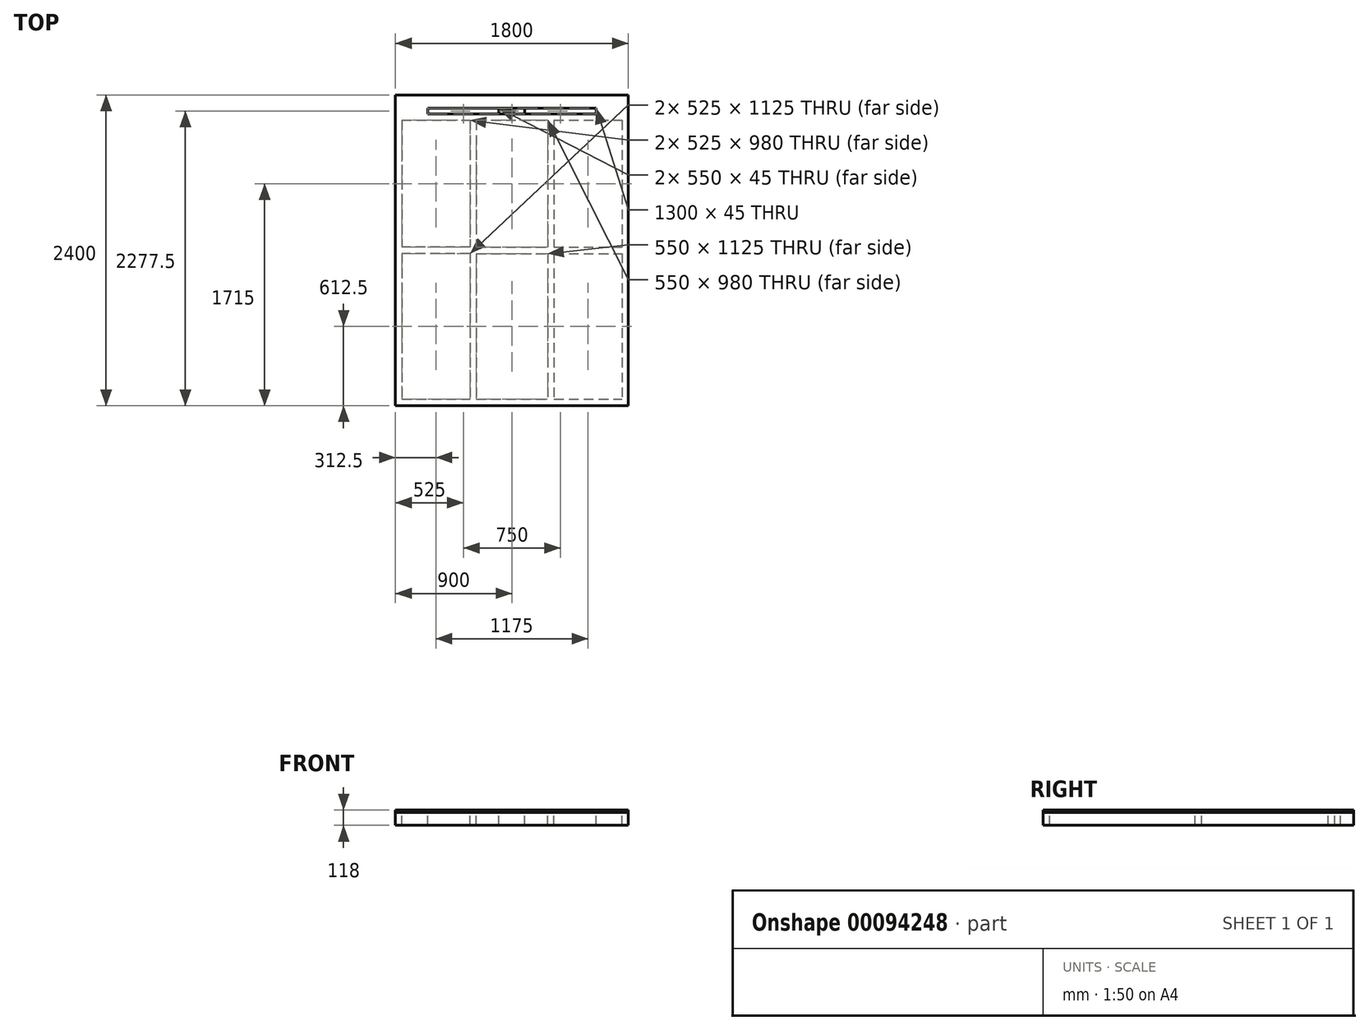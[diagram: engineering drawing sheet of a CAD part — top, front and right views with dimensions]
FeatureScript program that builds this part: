
annotation { "Feature Type Name" : "Feature", "Feature Type Description" : "" }
export const myFeature = defineFeature(function(context is Context, id is Id, definition is map)
    precondition{}
    {
        {
            var Q0;
            Q0=qCreatedBy(makeId("Top.planeOp"),FACE);
            var sketch = newSketch(context, id + "F0", { "sketchPlane" : qUnion([Q0])});
            skLineSegment(sketch, "E0.bottom", {"start": v(900, -1200) * mm, "end": v(-900, -1200) * mm});
            skLineSegment(sketch, "E0.top", {"start": v(900, 1200) * mm, "end": v(-900, 1200) * mm});
            skLineSegment(sketch, "E0.left", {"start": v(900, -1200) * mm, "end": v(900, 1200) * mm});
            skLineSegment(sketch, "E0.right", {"start": v(-900, -1200) * mm, "end": v(-900, 1200) * mm});
            skPoint(sketch, "E0.middle", {"position": v(0, 0) * mm});
            skLineSegment(sketch, "E1", {"start": v(-900, -1150) * mm, "end": v(900, -1150) * mm});
            skLineSegment(sketch, "E2", {"start": v(-900, 1150) * mm, "end": v(900, 1150) * mm});
            skLineSegment(sketch, "E3", {"start": v(-850, 1150) * mm, "end": v(-850, -1150) * mm});
            skLineSegment(sketch, "E4", {"start": v(-1110.96, 0) * mm, "end": v(1267.85, 0) * mm, "construction": true});
            skLineSegment(sketch, "E5", {"start": v(-325, 25) * mm, "end": v(-850, 25) * mm});
            skLineSegment(sketch, "E6", {"start": v(-325, -25) * mm, "end": v(-850, -25) * mm});
            skLineSegment(sketch, "E7", {"start": v(0, 1506.41) * mm, "end": v(0, -1337.08) * mm, "construction": true});
            skLineSegment(sketch, "E8", {"start": v(-275, 25) * mm, "end": v(0, 25) * mm});
            skLineSegment(sketch, "E9", {"start": v(-275, -25) * mm, "end": v(0, -25) * mm});
            skLineSegment(sketch, "E10", {"start": v(-300, 1299.82) * mm, "end": v(-300, -1330.47) * mm, "construction": true});
            skLineSegment(sketch, "E11.MirrorCS", {"start": v(300, 1299.82) * mm, "end": v(300, -1330.47) * mm, "construction": true});
            skLineSegment(sketch, "E12.MirrorCS", {"start": v(-275, 1005) * mm, "end": v(-275, -1150) * mm});
            skLineSegment(sketch, "E13.MirrorCS", {"start": v(275, 1005) * mm, "end": v(275, -1150) * mm});
            skLineSegment(sketch, "E14.MirrorCS", {"start": v(325, 1005) * mm, "end": v(325, -1150) * mm});
            skLineSegment(sketch, "E15.MirrorCS", {"start": v(275, 25) * mm, "end": v(0, 25) * mm});
            skLineSegment(sketch, "E16.MirrorCS", {"start": v(275, -25) * mm, "end": v(0, -25) * mm});
            skLineSegment(sketch, "E17.MirrorCS", {"start": v(325, -25) * mm, "end": v(850, -25) * mm});
            skLineSegment(sketch, "E18.MirrorCS", {"start": v(325, 25) * mm, "end": v(850, 25) * mm});
            skLineSegment(sketch, "E19.MirrorCS", {"start": v(850, 1150) * mm, "end": v(850, -1150) * mm});
            skLineSegment(sketch, "E20", {"start": v(-850, 1100) * mm, "end": v(850, 1100) * mm});
            skLineSegment(sketch, "E21", {"start": v(-850, 1055) * mm, "end": v(850, 1055) * mm});
            skLineSegment(sketch, "E22", {"start": v(-850, 1005) * mm, "end": v(850, 1005) * mm});
            skLineSegment(sketch, "E23", {"start": v(-650, 1055) * mm, "end": v(-650, 1100) * mm});
            skLineSegment(sketch, "E24.MirrorCS", {"start": v(650, 1055) * mm, "end": v(650, 1100) * mm});
            skLineSegment(sketch, "E25", {"start": v(-100, 1055) * mm, "end": v(-100, 1100) * mm});
            skLineSegment(sketch, "E26.MirrorCS", {"start": v(100, 1055) * mm, "end": v(100, 1100) * mm});
            skLineSegment(sketch, "E27.trimOffspring", {"start": v(-325, 1005) * mm, "end": v(-325, -1150) * mm});
            skSolve(sketch);
        }
        {
            var Q0;
            {var subQ4=sQuery(id+"F0.wireOp",EDGE,"E1");var subQ5=sQuery(id+"F0.wireOp",EDGE,"E0.left");var subQ6=makeQuery(id+"F0.imprint","INTERSECT",VERTEX,{"derivedFrom":[subQ5,subQ4]});Q0=makeQuery(id+"F0.imprint","IMPRINT",FACE,{"disambiguationData":[TD([[makeQuery(id+"F0.imprint","IMPRINT",EDGE,{"disambiguationData":[TD([[subQ6,-1.0]])],"derivedFrom":subQ5}),1.0]])]});}
            var Q1;
            {var subQ4=sQuery(id+"F0.wireOp",EDGE,"E0.bottom");Q1=makeQuery(id+"F0.imprint","IMPRINT",FACE,{"disambiguationData":[TD([[makeQuery(id+"F0.imprint","IMPRINT",EDGE,{"derivedFrom":subQ4}),-1.0]])]});}
            var Q2;
            {var subQ4=sQuery(id+"F0.wireOp",EDGE,"E0.right");var subQ6=sQuery(id+"F0.wireOp",EDGE,"E1");var subQ7=makeQuery(id+"F0.imprint","INTERSECT",VERTEX,{"derivedFrom":[subQ4,subQ6]});Q2=makeQuery(id+"F0.imprint","IMPRINT",FACE,{"disambiguationData":[TD([[makeQuery(id+"F0.imprint","IMPRINT",EDGE,{"disambiguationData":[TD([[subQ7,-1.0]])],"derivedFrom":subQ4}),-1.0]])]});}
            var Q3;
            {var subQ0=sQuery(id+"F0.wireOp",EDGE,"E5");Q3=makeQuery(id+"F0.imprint","IMPRINT",FACE,{"disambiguationData":[TD([[makeQuery(id+"F0.imprint","IMPRINT",EDGE,{"derivedFrom":subQ0}),1.0]])]});}
            var Q4;
            {var subQ4=sQuery(id+"F0.wireOp",EDGE,"E8");Q4=makeQuery(id+"F0.imprint","IMPRINT",FACE,{"disambiguationData":[TD([[makeQuery(id+"F0.imprint","IMPRINT",EDGE,{"derivedFrom":subQ4}),-1.0]])]});}
            var Q5;
            {var subQ0=sQuery(id+"F0.wireOp",EDGE,"E13.MirrorCS");var subQ1=sQuery(id+"F0.wireOp",EDGE,"E1");var subQ2=makeQuery(id+"F0.imprint","INTERSECT",VERTEX,{"derivedFrom":[subQ1,subQ0]});Q5=makeQuery(id+"F0.imprint","IMPRINT",FACE,{"disambiguationData":[TD([[makeQuery(id+"F0.imprint","IMPRINT",EDGE,{"disambiguationData":[TD([[subQ2,-1.0]])],"derivedFrom":subQ1}),1.0]])]});}
            var Q6;
            {var subQ0=sQuery(id+"F0.wireOp",EDGE,"E17.MirrorCS");Q6=makeQuery(id+"F0.imprint","IMPRINT",FACE,{"disambiguationData":[TD([[makeQuery(id+"F0.imprint","IMPRINT",EDGE,{"derivedFrom":subQ0}),1.0]])]});}
            var Q7;
            {var subQ4=sQuery(id+"F0.wireOp",EDGE,"E0.top");Q7=makeQuery(id+"F0.imprint","IMPRINT",FACE,{"disambiguationData":[TD([[makeQuery(id+"F0.imprint","IMPRINT",EDGE,{"derivedFrom":subQ4}),1.0]])]});}
            var Q8;
            {var subQ1=sQuery(id+"F0.wireOp",EDGE,"E3");var subQ4=sQuery(id+"F0.wireOp",EDGE,"E21");var subQ10=makeQuery(id+"F0.imprint","INTERSECT",VERTEX,{"derivedFrom":[subQ1,subQ4]});Q8=makeQuery(id+"F0.imprint","IMPRINT",FACE,{"disambiguationData":[TD([[makeQuery(id+"F0.imprint","IMPRINT",EDGE,{"disambiguationData":[TD([[subQ10,-1.0]])],"derivedFrom":subQ1}),1.0]])]});}
            var Q9;
            {var subQ0=sQuery(id+"F0.wireOp",EDGE,"E13.MirrorCS");var subQ1=sQuery(id+"F0.wireOp",EDGE,"E1");var subQ2=makeQuery(id+"F0.imprint","INTERSECT",VERTEX,{"derivedFrom":[subQ1,subQ0]});Q9=makeQuery(id+"F0.imprint","IMPRINT",FACE,{"disambiguationData":[TD([[makeQuery(id+"F0.imprint","IMPRINT",EDGE,{"disambiguationData":[TD([[subQ2,-1.0]])],"derivedFrom":subQ1}),1.0]])]});}
            var Q10;
            {var subQ0=sQuery(id+"F0.wireOp",EDGE,"E17.MirrorCS");Q10=makeQuery(id+"F0.imprint","IMPRINT",FACE,{"disambiguationData":[TD([[makeQuery(id+"F0.imprint","IMPRINT",EDGE,{"derivedFrom":subQ0}),1.0]])]});}
            var Q11;
            {var subQ1=sQuery(id+"F0.wireOp",EDGE,"E3");var subQ5=sQuery(id+"F0.wireOp",EDGE,"E2");var subQ8=makeQuery(id+"F0.imprint","INTERSECT",VERTEX,{"derivedFrom":[subQ5,subQ1]});Q11=makeQuery(id+"F0.imprint","IMPRINT",FACE,{"disambiguationData":[TD([[makeQuery(id+"F0.imprint","IMPRINT",EDGE,{"disambiguationData":[TD([[subQ8,-1.0]])],"derivedFrom":subQ5}),-1.0]])]});}
            var Q12;
            {var subQ1=sQuery(id+"F0.wireOp",EDGE,"E3");var subQ5=sQuery(id+"F0.wireOp",EDGE,"E2");var subQ8=makeQuery(id+"F0.imprint","INTERSECT",VERTEX,{"derivedFrom":[subQ5,subQ1]});Q12=makeQuery(id+"F0.imprint","IMPRINT",FACE,{"disambiguationData":[TD([[makeQuery(id+"F0.imprint","IMPRINT",EDGE,{"disambiguationData":[TD([[subQ8,-1.0]])],"derivedFrom":subQ5}),-1.0]])]});}
            var Q13;
            {var subQ1=sQuery(id+"F0.wireOp",EDGE,"E3");var subQ5=sQuery(id+"F0.wireOp",EDGE,"E2");var subQ8=makeQuery(id+"F0.imprint","INTERSECT",VERTEX,{"derivedFrom":[subQ5,subQ1]});Q13=makeQuery(id+"F0.imprint","IMPRINT",FACE,{"disambiguationData":[TD([[makeQuery(id+"F0.imprint","IMPRINT",EDGE,{"disambiguationData":[TD([[subQ8,-1.0]])],"derivedFrom":subQ5}),-1.0]])]});}
            var Q14;
            {var subQ1=sQuery(id+"F0.wireOp",EDGE,"E3");var subQ5=sQuery(id+"F0.wireOp",EDGE,"E2");var subQ8=makeQuery(id+"F0.imprint","INTERSECT",VERTEX,{"derivedFrom":[subQ5,subQ1]});Q14=makeQuery(id+"F0.imprint","IMPRINT",FACE,{"disambiguationData":[TD([[makeQuery(id+"F0.imprint","IMPRINT",EDGE,{"disambiguationData":[TD([[subQ8,-1.0]])],"derivedFrom":subQ5}),-1.0]])]});}
            var Q15;
            {var subQ1=sQuery(id+"F0.wireOp",EDGE,"E3");var subQ5=sQuery(id+"F0.wireOp",EDGE,"E2");var subQ8=makeQuery(id+"F0.imprint","INTERSECT",VERTEX,{"derivedFrom":[subQ5,subQ1]});Q15=makeQuery(id+"F0.imprint","IMPRINT",FACE,{"disambiguationData":[TD([[makeQuery(id+"F0.imprint","IMPRINT",EDGE,{"disambiguationData":[TD([[subQ8,-1.0]])],"derivedFrom":subQ5}),-1.0]])]});}
            var Q16;
            {var subQ5=sQuery(id+"F0.wireOp",EDGE,"E23");Q16=makeQuery(id+"F0.imprint","IMPRINT",FACE,{"disambiguationData":[TD([[makeQuery(id+"F0.imprint","IMPRINT",EDGE,{"derivedFrom":subQ5}),1.0]])]});}
            var Q17;
            {var subQ0=sQuery(id+"F0.wireOp",EDGE,"E25");Q17=makeQuery(id+"F0.imprint","IMPRINT",FACE,{"disambiguationData":[TD([[makeQuery(id+"F0.imprint","IMPRINT",EDGE,{"derivedFrom":subQ0}),-1.0]])]});}
            var Q18;
            {var subQ5=sQuery(id+"F0.wireOp",EDGE,"E24.MirrorCS");Q18=makeQuery(id+"F0.imprint","IMPRINT",FACE,{"disambiguationData":[TD([[makeQuery(id+"F0.imprint","IMPRINT",EDGE,{"derivedFrom":subQ5}),-1.0]])]});}
            var Q19;
            {var subQ0=sQuery(id+"F0.wireOp",EDGE,"E12.MirrorCS");var subQ2=sQuery(id+"F0.wireOp",EDGE,"E1");var subQ3=makeQuery(id+"F0.imprint","INTERSECT",VERTEX,{"derivedFrom":[subQ2,subQ0]});Q19=makeQuery(id+"F0.imprint","IMPRINT",FACE,{"disambiguationData":[TD([[makeQuery(id+"F0.imprint","IMPRINT",EDGE,{"disambiguationData":[TD([[subQ3,1.0]])],"derivedFrom":subQ2}),1.0]])]});}
            extrude(context, id + "F1", {"entities" : qUnion([Q0, Q1, Q2, Q3, Q4, Q5, Q6, Q7, Q8, Q9, Q10, Q11, Q12, Q13, Q14, Q15, Q16, Q17, Q18, Q19]), "oppositeDirection" : true, "depth" : 100 * mm});
        }
        {
            var Q0;
            {var subQ5=sQuery(id+"F0.wireOp",EDGE,"E6");Q0=makeQuery(id+"F0.imprint","IMPRINT",FACE,{"disambiguationData":[TD([[makeQuery(id+"F0.imprint","IMPRINT",EDGE,{"derivedFrom":subQ5}),1.0]])]});}
            var Q1;
            {var subQ1=sQuery(id+"F0.wireOp",EDGE,"E9");Q1=makeQuery(id+"F0.imprint","IMPRINT",FACE,{"disambiguationData":[TD([[makeQuery(id+"F0.imprint","IMPRINT",EDGE,{"derivedFrom":subQ1}),-1.0]])]});}
            var Q2;
            {var subQ5=sQuery(id+"F0.wireOp",EDGE,"E17.MirrorCS");Q2=makeQuery(id+"F0.imprint","IMPRINT",FACE,{"disambiguationData":[TD([[makeQuery(id+"F0.imprint","IMPRINT",EDGE,{"derivedFrom":subQ5}),-1.0]])]});}
            var Q3;
            {var subQ0=sQuery(id+"F0.wireOp",EDGE,"E5");Q3=makeQuery(id+"F0.imprint","IMPRINT",FACE,{"disambiguationData":[TD([[makeQuery(id+"F0.imprint","IMPRINT",EDGE,{"derivedFrom":subQ0}),-1.0]])]});}
            var Q4;
            {var subQ5=sQuery(id+"F0.wireOp",EDGE,"E8");Q4=makeQuery(id+"F0.imprint","IMPRINT",FACE,{"disambiguationData":[TD([[makeQuery(id+"F0.imprint","IMPRINT",EDGE,{"derivedFrom":subQ5}),1.0]])]});}
            var Q5;
            {var subQ0=sQuery(id+"F0.wireOp",EDGE,"E18.MirrorCS");Q5=makeQuery(id+"F0.imprint","IMPRINT",FACE,{"disambiguationData":[TD([[makeQuery(id+"F0.imprint","IMPRINT",EDGE,{"derivedFrom":subQ0}),1.0]])]});}
            var Q6;
            {var subQ0=sQuery(id+"F0.wireOp",EDGE,"E20");var subQ1=sQuery(id+"F0.wireOp",EDGE,"JPLQ0b7U-AVgE-R2Rs-OC7f-LN1T8d5NPDnQ");var subQ2=makeQuery(id+"F0.imprint","INTERSECT",VERTEX,{"derivedFrom":[subQ1,subQ0]});Q6=makeQuery(id+"F0.imprint","IMPRINT",FACE,{"disambiguationData":[TD([[makeQuery(id+"F0.imprint","IMPRINT",EDGE,{"disambiguationData":[TD([[subQ2,-1.0]])],"derivedFrom":subQ1}),1.0]])]});}
            var Q7;
            {var subQ0=sQuery(id+"F0.wireOp",EDGE,"E20");var subQ1=sQuery(id+"F0.wireOp",EDGE,"E13.MirrorCS");var subQ2=makeQuery(id+"F0.imprint","INTERSECT",VERTEX,{"derivedFrom":[subQ1,subQ0]});Q7=makeQuery(id+"F0.imprint","IMPRINT",FACE,{"disambiguationData":[TD([[makeQuery(id+"F0.imprint","IMPRINT",EDGE,{"disambiguationData":[TD([[subQ2,-1.0]])],"derivedFrom":subQ1}),1.0]])]});}
            var Q8;
            {var subQ5=sQuery(id+"F0.wireOp",EDGE,"E24.MirrorCS");Q8=makeQuery(id+"F0.imprint","IMPRINT",FACE,{"disambiguationData":[TD([[makeQuery(id+"F0.imprint","IMPRINT",EDGE,{"derivedFrom":subQ5}),-1.0]])]});}
            var Q9;
            {var subQ1=sQuery(id+"F0.wireOp",EDGE,"E0.left");var subQ6=sQuery(id+"F0.wireOp",EDGE,"E1");var subQ7=makeQuery(id+"F0.imprint","INTERSECT",VERTEX,{"derivedFrom":[subQ1,subQ6]});Q9=makeQuery(id+"F0.imprint","IMPRINT",FACE,{"disambiguationData":[TD([[makeQuery(id+"F0.imprint","IMPRINT",EDGE,{"disambiguationData":[TD([[subQ7,-1.0]])],"derivedFrom":subQ1}),1.0]])]});}
            var Q10;
            {var subQ4=sQuery(id+"F0.wireOp",EDGE,"E0.top");Q10=makeQuery(id+"F0.imprint","IMPRINT",FACE,{"disambiguationData":[TD([[makeQuery(id+"F0.imprint","IMPRINT",EDGE,{"derivedFrom":subQ4}),1.0]])]});}
            var Q11;
            {var subQ0=sQuery(id+"F0.wireOp",EDGE,"E21");var subQ4=sQuery(id+"F0.wireOp",EDGE,"E14.MirrorCS");var subQ5=makeQuery(id+"F0.imprint","INTERSECT",VERTEX,{"derivedFrom":[subQ4,subQ0]});Q11=makeQuery(id+"F0.imprint","IMPRINT",FACE,{"disambiguationData":[TD([[makeQuery(id+"F0.imprint","IMPRINT",EDGE,{"disambiguationData":[TD([[subQ5,-1.0]])],"derivedFrom":subQ4}),1.0]])]});}
            var Q12;
            {var subQ2=sQuery(id+"F0.wireOp",EDGE,"E14.MirrorCS");var subQ5=sQuery(id+"F0.wireOp",EDGE,"E2");var subQ8=makeQuery(id+"F0.imprint","INTERSECT",VERTEX,{"derivedFrom":[subQ5,subQ2]});Q12=makeQuery(id+"F0.imprint","IMPRINT",FACE,{"disambiguationData":[TD([[makeQuery(id+"F0.imprint","IMPRINT",EDGE,{"disambiguationData":[TD([[subQ8,-1.0]])],"derivedFrom":subQ5}),-1.0]])]});}
            var Q13;
            {var subQ1=sQuery(id+"F0.wireOp",EDGE,"E2");var subQ6=sQuery(id+"F0.wireOp",EDGE,"E12.MirrorCS");var subQ8=makeQuery(id+"F0.imprint","INTERSECT",VERTEX,{"derivedFrom":[subQ1,subQ6]});Q13=makeQuery(id+"F0.imprint","IMPRINT",FACE,{"disambiguationData":[TD([[makeQuery(id+"F0.imprint","IMPRINT",EDGE,{"disambiguationData":[TD([[subQ8,-1.0]])],"derivedFrom":subQ1}),-1.0]])]});}
            var Q14;
            {var subQ0=sQuery(id+"F0.wireOp",EDGE,"E21");var subQ4=sQuery(id+"F0.wireOp",EDGE,"E12.MirrorCS");var subQ8=makeQuery(id+"F0.imprint","INTERSECT",VERTEX,{"derivedFrom":[subQ4,subQ0]});Q14=makeQuery(id+"F0.imprint","IMPRINT",FACE,{"disambiguationData":[TD([[makeQuery(id+"F0.imprint","IMPRINT",EDGE,{"disambiguationData":[TD([[subQ8,-1.0]])],"derivedFrom":subQ4}),1.0]])]});}
            var Q15;
            {var subQ0=sQuery(id+"F0.wireOp",EDGE,"E13.MirrorCS");var subQ1=sQuery(id+"F0.wireOp",EDGE,"E2");var subQ2=makeQuery(id+"F0.imprint","INTERSECT",VERTEX,{"derivedFrom":[subQ1,subQ0]});Q15=makeQuery(id+"F0.imprint","IMPRINT",FACE,{"disambiguationData":[TD([[makeQuery(id+"F0.imprint","IMPRINT",EDGE,{"disambiguationData":[TD([[subQ2,-1.0]])],"derivedFrom":subQ1}),-1.0]])]});}
            var Q16;
            {var subQ0=sQuery(id+"F0.wireOp",EDGE,"E21");var subQ1=sQuery(id+"F0.wireOp",EDGE,"E13.MirrorCS");var subQ2=makeQuery(id+"F0.imprint","INTERSECT",VERTEX,{"derivedFrom":[subQ1,subQ0]});Q16=makeQuery(id+"F0.imprint","IMPRINT",FACE,{"disambiguationData":[TD([[makeQuery(id+"F0.imprint","IMPRINT",EDGE,{"disambiguationData":[TD([[subQ2,-1.0]])],"derivedFrom":subQ1}),1.0]])]});}
            var Q17;
            {var subQ1=sQuery(id+"F0.wireOp",EDGE,"E2");var subQ5=sQuery(id+"F0.wireOp",EDGE,"E3");var subQ8=makeQuery(id+"F0.imprint","INTERSECT",VERTEX,{"derivedFrom":[subQ1,subQ5]});Q17=makeQuery(id+"F0.imprint","IMPRINT",FACE,{"disambiguationData":[TD([[makeQuery(id+"F0.imprint","IMPRINT",EDGE,{"disambiguationData":[TD([[subQ8,-1.0]])],"derivedFrom":subQ1}),-1.0]])]});}
            var Q18;
            {var subQ0=sQuery(id+"F0.wireOp",EDGE,"JPLQ0b7U-AVgE-R2Rs-OC7f-LN1T8d5NPDnQ");var subQ1=sQuery(id+"F0.wireOp",EDGE,"E2");var subQ2=makeQuery(id+"F0.imprint","INTERSECT",VERTEX,{"derivedFrom":[subQ1,subQ0]});Q18=makeQuery(id+"F0.imprint","IMPRINT",FACE,{"disambiguationData":[TD([[makeQuery(id+"F0.imprint","IMPRINT",EDGE,{"disambiguationData":[TD([[subQ2,-1.0]])],"derivedFrom":subQ1}),-1.0]])]});}
            var Q19;
            {var subQ1=sQuery(id+"F0.wireOp",EDGE,"E0.right");var subQ7=sQuery(id+"F0.wireOp",EDGE,"E1");var subQ8=makeQuery(id+"F0.imprint","INTERSECT",VERTEX,{"derivedFrom":[subQ1,subQ7]});Q19=makeQuery(id+"F0.imprint","IMPRINT",FACE,{"disambiguationData":[TD([[makeQuery(id+"F0.imprint","IMPRINT",EDGE,{"disambiguationData":[TD([[subQ8,-1.0]])],"derivedFrom":subQ1}),-1.0]])]});}
            var Q20;
            {var subQ5=sQuery(id+"F0.wireOp",EDGE,"E23");Q20=makeQuery(id+"F0.imprint","IMPRINT",FACE,{"disambiguationData":[TD([[makeQuery(id+"F0.imprint","IMPRINT",EDGE,{"derivedFrom":subQ5}),1.0]])]});}
            var Q21;
            {var subQ0=sQuery(id+"F0.wireOp",EDGE,"E21");var subQ4=sQuery(id+"F0.wireOp",EDGE,"E3");var subQ5=makeQuery(id+"F0.imprint","INTERSECT",VERTEX,{"derivedFrom":[subQ4,subQ0]});Q21=makeQuery(id+"F0.imprint","IMPRINT",FACE,{"disambiguationData":[TD([[makeQuery(id+"F0.imprint","IMPRINT",EDGE,{"disambiguationData":[TD([[subQ5,-1.0]])],"derivedFrom":subQ4}),1.0]])]});}
            var Q22;
            {var subQ0=sQuery(id+"F0.wireOp",EDGE,"E21");var subQ1=sQuery(id+"F0.wireOp",EDGE,"JPLQ0b7U-AVgE-R2Rs-OC7f-LN1T8d5NPDnQ");var subQ2=makeQuery(id+"F0.imprint","INTERSECT",VERTEX,{"derivedFrom":[subQ1,subQ0]});Q22=makeQuery(id+"F0.imprint","IMPRINT",FACE,{"disambiguationData":[TD([[makeQuery(id+"F0.imprint","IMPRINT",EDGE,{"disambiguationData":[TD([[subQ2,-1.0]])],"derivedFrom":subQ1}),1.0]])]});}
            var Q23;
            {var subQ0=sQuery(id+"F0.wireOp",EDGE,"JPLQ0b7U-AVgE-R2Rs-OC7f-LN1T8d5NPDnQ");var subQ1=sQuery(id+"F0.wireOp",EDGE,"E1");var subQ2=makeQuery(id+"F0.imprint","INTERSECT",VERTEX,{"derivedFrom":[subQ1,subQ0]});Q23=makeQuery(id+"F0.imprint","IMPRINT",FACE,{"disambiguationData":[TD([[makeQuery(id+"F0.imprint","IMPRINT",EDGE,{"disambiguationData":[TD([[subQ2,-1.0]])],"derivedFrom":subQ1}),1.0]])]});}
            var Q24;
            {var subQ0=sQuery(id+"F0.wireOp",EDGE,"E5");Q24=makeQuery(id+"F0.imprint","IMPRINT",FACE,{"disambiguationData":[TD([[makeQuery(id+"F0.imprint","IMPRINT",EDGE,{"derivedFrom":subQ0}),1.0]])]});}
            var Q25;
            {var subQ5=sQuery(id+"F0.wireOp",EDGE,"E8");Q25=makeQuery(id+"F0.imprint","IMPRINT",FACE,{"disambiguationData":[TD([[makeQuery(id+"F0.imprint","IMPRINT",EDGE,{"derivedFrom":subQ5}),-1.0]])]});}
            var Q26;
            {var subQ0=sQuery(id+"F0.wireOp",EDGE,"E13.MirrorCS");var subQ1=sQuery(id+"F0.wireOp",EDGE,"E1");var subQ2=makeQuery(id+"F0.imprint","INTERSECT",VERTEX,{"derivedFrom":[subQ1,subQ0]});Q26=makeQuery(id+"F0.imprint","IMPRINT",FACE,{"disambiguationData":[TD([[makeQuery(id+"F0.imprint","IMPRINT",EDGE,{"disambiguationData":[TD([[subQ2,-1.0]])],"derivedFrom":subQ1}),1.0]])]});}
            var Q27;
            {var subQ0=sQuery(id+"F0.wireOp",EDGE,"E17.MirrorCS");Q27=makeQuery(id+"F0.imprint","IMPRINT",FACE,{"disambiguationData":[TD([[makeQuery(id+"F0.imprint","IMPRINT",EDGE,{"derivedFrom":subQ0}),1.0]])]});}
            var Q28;
            {var subQ4=sQuery(id+"F0.wireOp",EDGE,"E0.bottom");Q28=makeQuery(id+"F0.imprint","IMPRINT",FACE,{"disambiguationData":[TD([[makeQuery(id+"F0.imprint","IMPRINT",EDGE,{"derivedFrom":subQ4}),-1.0]])]});}
            var Q29;
            {var subQ0=sQuery(id+"F0.wireOp",EDGE,"E12.MirrorCS");var subQ2=sQuery(id+"F0.wireOp",EDGE,"E1");var subQ3=makeQuery(id+"F0.imprint","INTERSECT",VERTEX,{"derivedFrom":[subQ2,subQ0]});Q29=makeQuery(id+"F0.imprint","IMPRINT",FACE,{"disambiguationData":[TD([[makeQuery(id+"F0.imprint","IMPRINT",EDGE,{"disambiguationData":[TD([[subQ3,1.0]])],"derivedFrom":subQ2}),1.0]])]});}
            extrude(context, id + "F2", {"entities" : qUnion([Q0, Q1, Q2, Q3, Q4, Q5, Q6, Q7, Q8, Q9, Q10, Q11, Q12, Q13, Q14, Q15, Q16, Q17, Q18, Q19, Q20, Q21, Q22, Q23, Q24, Q25, Q26, Q27, Q28, Q29]), "depth" : 18 * mm});
        }
    });
